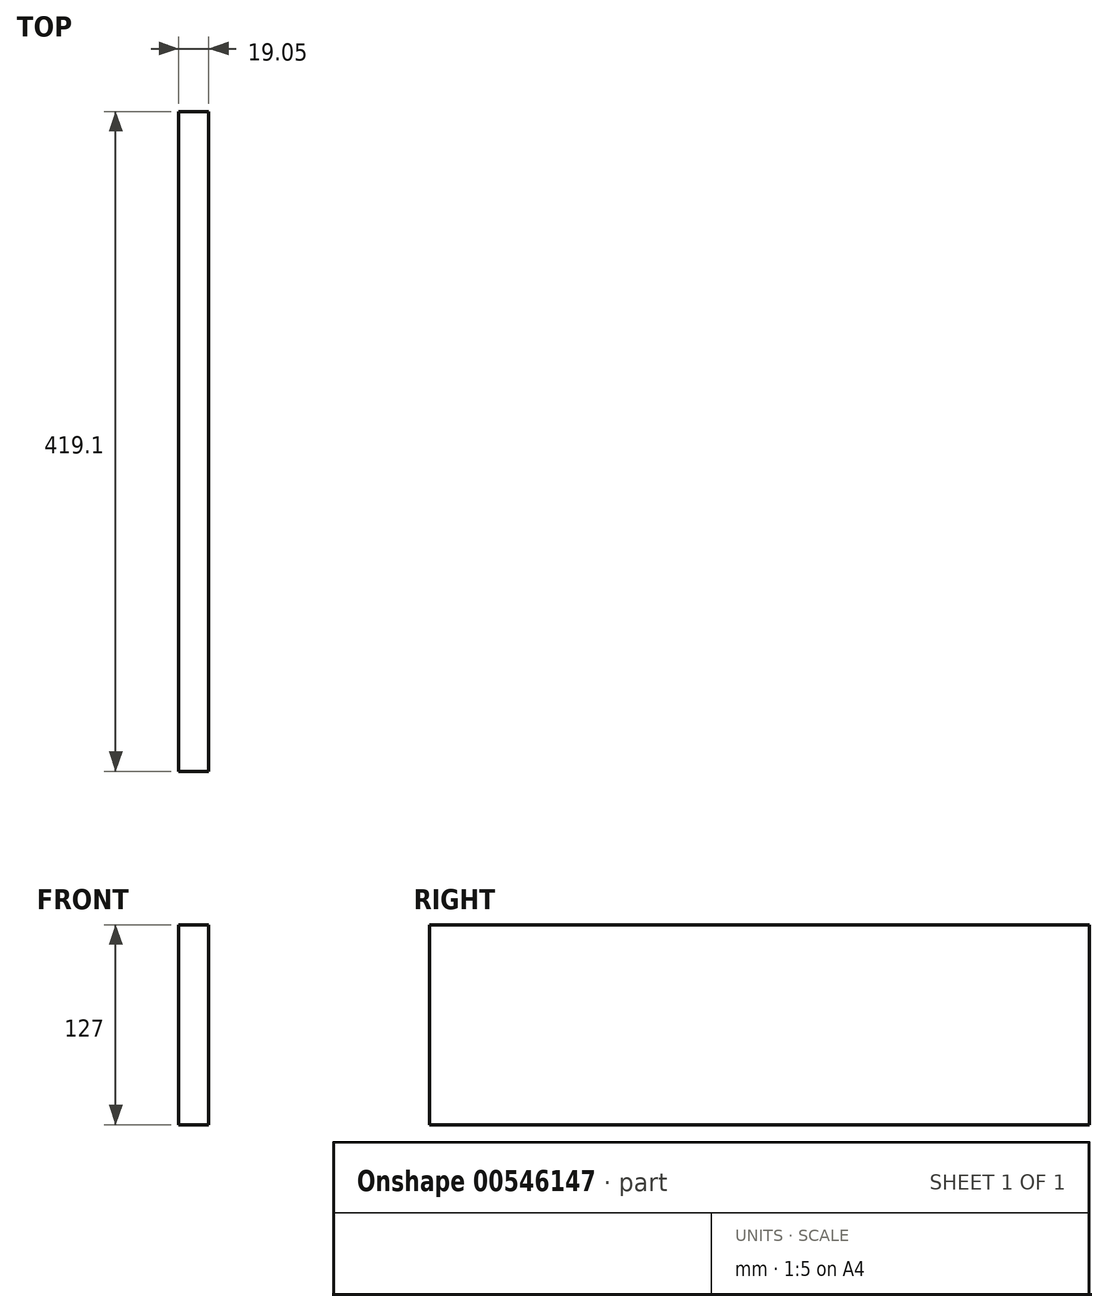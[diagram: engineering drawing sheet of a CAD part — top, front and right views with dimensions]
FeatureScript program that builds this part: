
annotation { "Feature Type Name" : "Feature", "Feature Type Description" : "" }
export const myFeature = defineFeature(function(context is Context, id is Id, definition is map)
    precondition{}
    {
        {
            var Q0;
            Q0=qCreatedBy(makeId("Right.planeOp"),FACE);
            var sketch = newSketch(context, id + "F0", { "sketchPlane" : qUnion([Q0])});
            skLineSegment(sketch, "E0.bottom", {"start": v(209.55, -63.5) * mm, "end": v(-209.55, -63.5) * mm});
            skLineSegment(sketch, "E0.top", {"start": v(209.55, 63.5) * mm, "end": v(-209.55, 63.5) * mm});
            skLineSegment(sketch, "E0.left", {"start": v(209.55, -63.5) * mm, "end": v(209.55, 63.5) * mm});
            skLineSegment(sketch, "E0.right", {"start": v(-209.55, -63.5) * mm, "end": v(-209.55, 63.5) * mm});
            skPoint(sketch, "E0.middle", {"position": v(0, 0) * mm});
            skSolve(sketch);
        }
        {
            var Q0;
            Q0 = qSketchRegion(id + "F0", true);
            extrude(context, id + "F1", {"entities" : qUnion([Q0]), "depth" : 19.05 * mm, "offsetDistance" : 25.4 * mm});
        }
    });
